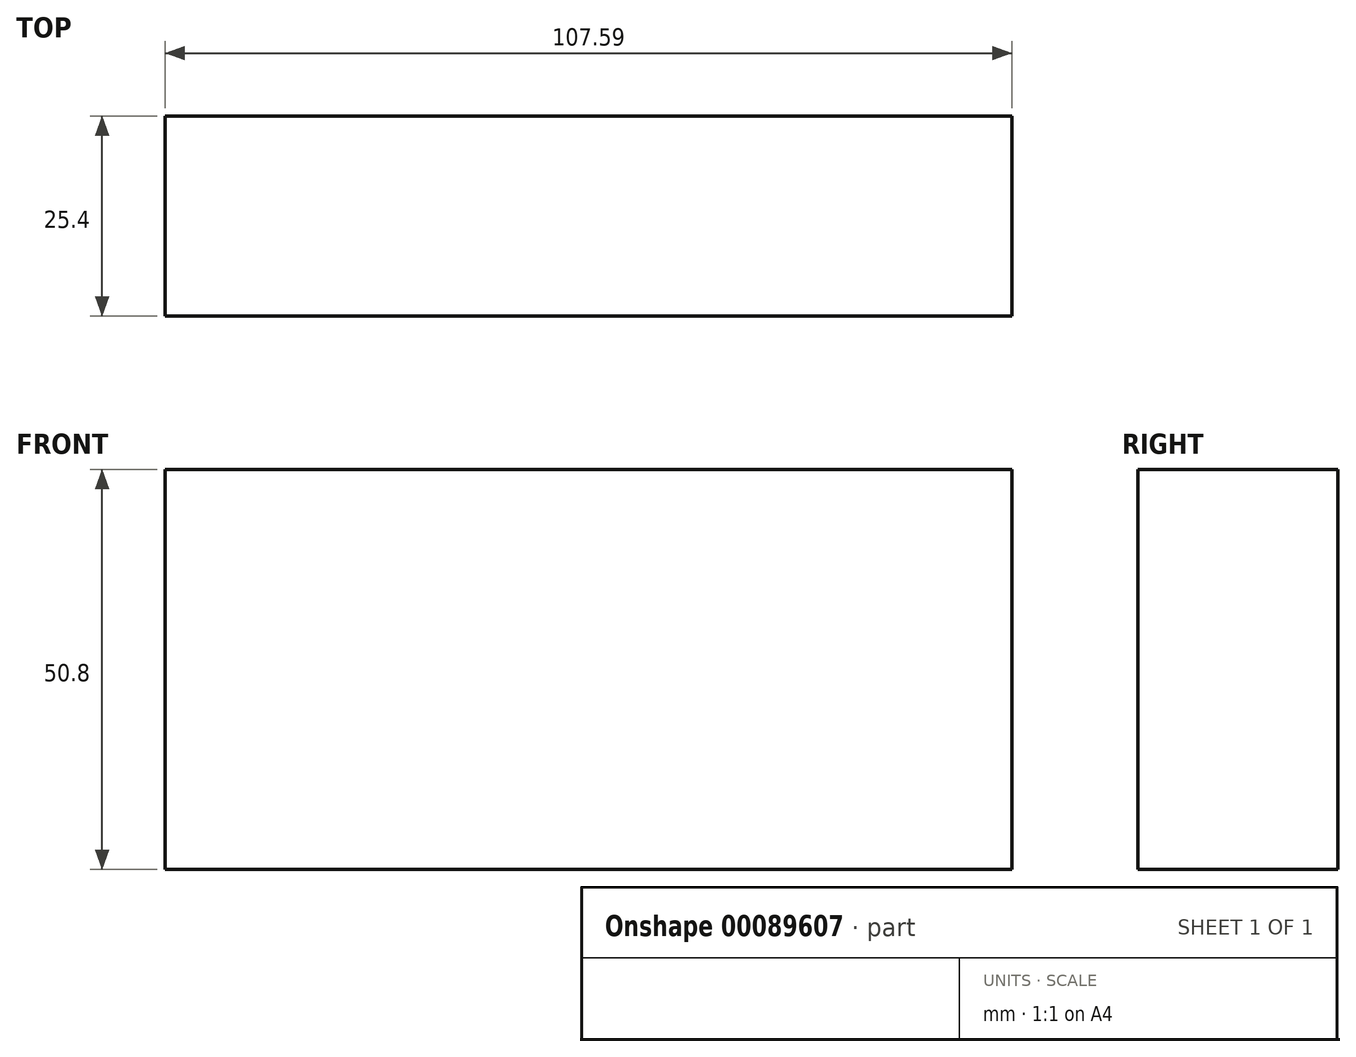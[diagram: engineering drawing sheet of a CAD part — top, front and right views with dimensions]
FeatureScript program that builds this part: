
annotation { "Feature Type Name" : "Feature", "Feature Type Description" : "" }
export const myFeature = defineFeature(function(context is Context, id is Id, definition is map)
    precondition{}
    {
        {
            var Q0;
            Q0=qCreatedBy(makeId("Front.planeOp"),FACE);
            var sketch = newSketch(context, id + "F0", { "sketchPlane" : qUnion([Q0])});
            skLineSegment(sketch, "E0", {"start": v(56.8, 25.4) * mm, "end": v(-50.8, 25.4) * mm});
            skLineSegment(sketch, "E1", {"start": v(-50.8, 25.4) * mm, "end": v(-50.8, -25.4) * mm});
            skLineSegment(sketch, "E2", {"start": v(-50.8, -25.4) * mm, "end": v(56.8, -25.4) * mm});
            skLineSegment(sketch, "E3", {"start": v(56.8, 25.4) * mm, "end": v(56.8, -25.4) * mm});
            skSolve(sketch);
        }
        {
            var Q0;
            Q0=makeQuery(id+"F0.imprint","IMPRINT",FACE,{"disambiguationData":[TD([[makeQuery(id+"F0.imprint","IMPRINT",EDGE,{"derivedFrom":sQuery(id+"F0.wireOp",EDGE,"E0")}),1.0]])]});
            extrude(context, id + "F1", {"entities" : qUnion([Q0]), "depth" : 25.4 * mm});
        }
    });
